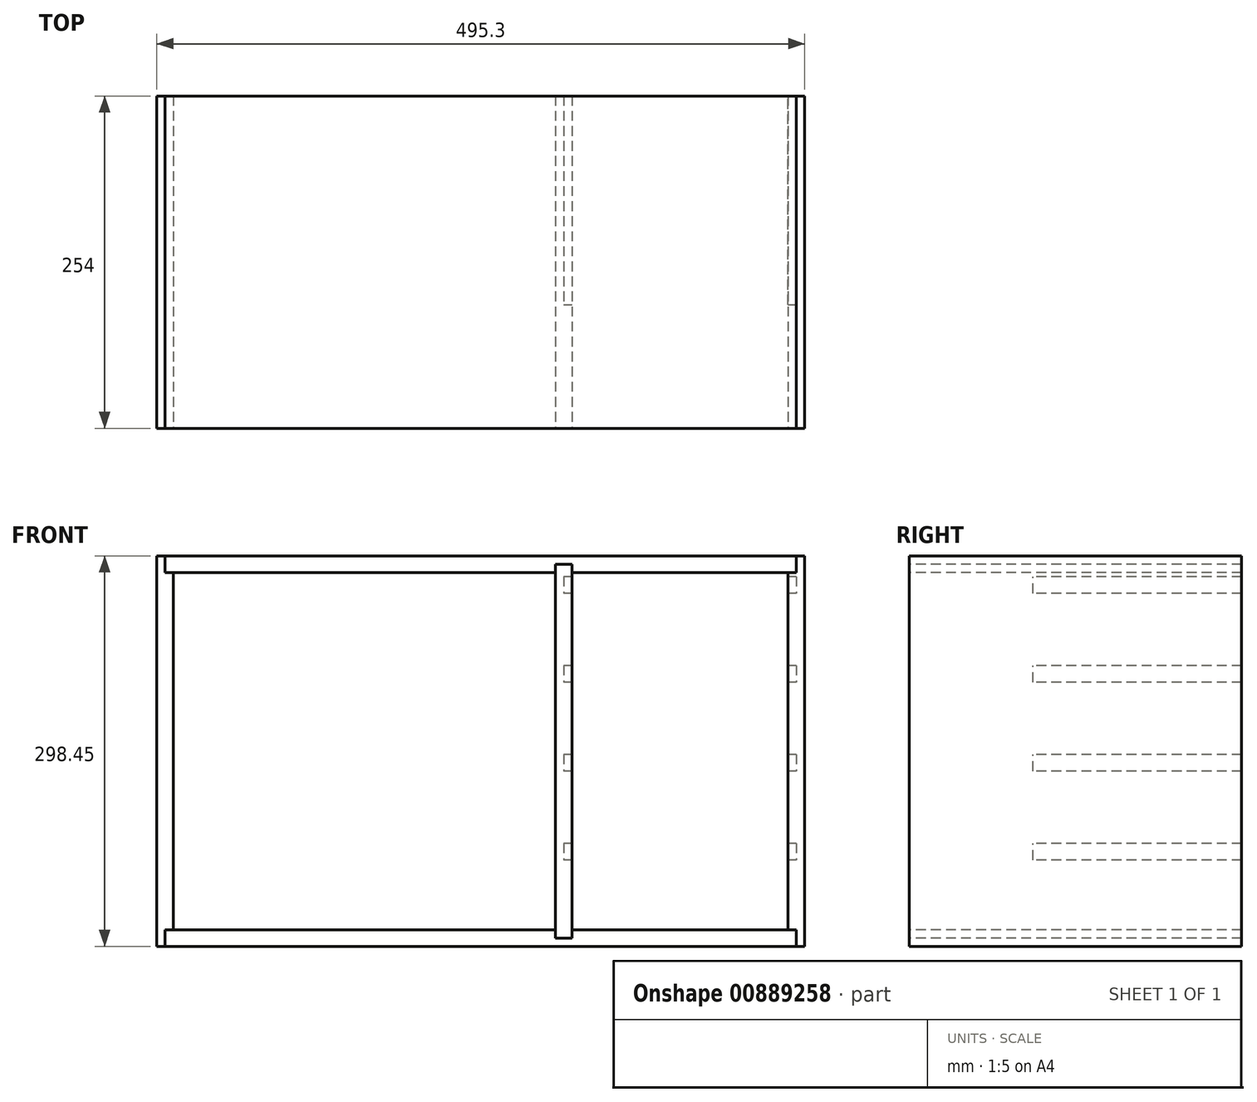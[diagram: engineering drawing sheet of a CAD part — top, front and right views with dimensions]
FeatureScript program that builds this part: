
annotation { "Feature Type Name" : "Feature", "Feature Type Description" : "" }
export const myFeature = defineFeature(function(context is Context, id is Id, definition is map)
    precondition{}
    {
        {
            var Q0;
            Q0=qCreatedBy(makeId("Front.planeOp"),FACE);
            var sketch = newSketch(context, id + "F0", { "sketchPlane" : qUnion([Q0])});
            skLineSegment(sketch, "E0.bottom", {"start": v(0, 0) * mm, "end": v(495.3, 0) * mm});
            skLineSegment(sketch, "E0.top", {"start": v(0, 298.45) * mm, "end": v(495.3, 298.45) * mm});
            skLineSegment(sketch, "E0.left", {"start": v(0, 0) * mm, "end": v(0, 298.45) * mm});
            skLineSegment(sketch, "E0.right", {"start": v(495.3, 0) * mm, "end": v(495.3, 298.45) * mm});
            skLineSegment(sketch, "E1.0", {"start": v(12.7, 285.75) * mm, "end": v(482.6, 285.75) * mm});
            skLineSegment(sketch, "E1.1", {"start": v(12.7, 12.7) * mm, "end": v(12.7, 285.75) * mm});
            skLineSegment(sketch, "E1.2", {"start": v(12.7, 12.7) * mm, "end": v(482.6, 12.7) * mm});
            skLineSegment(sketch, "E1.3", {"start": v(482.6, 12.7) * mm, "end": v(482.6, 285.75) * mm});
            skLineSegment(sketch, "E2", {"start": v(311.15, 12.7) * mm, "end": v(311.15, 285.75) * mm, "construction": true});
            skLineSegment(sketch, "E3.0", {"start": v(317.5, 12.7) * mm, "end": v(317.5, 285.75) * mm, "construction": true});
            skLineSegment(sketch, "E4.0", {"start": v(304.8, 12.7) * mm, "end": v(304.8, 285.75) * mm, "construction": true});
            skLineSegment(sketch, "E5", {"start": v(12.7, 44.45) * mm, "end": v(304.8, 44.45) * mm, "construction": true});
            skLineSegment(sketch, "E6.0.1.0", {"start": v(12.7, 76.2) * mm, "end": v(304.8, 76.2) * mm, "construction": true});
            skLineSegment(sketch, "E6.0.2.0", {"start": v(12.7, 107.95) * mm, "end": v(304.8, 107.95) * mm, "construction": true});
            skLineSegment(sketch, "E6.0.3.0", {"start": v(12.7, 139.7) * mm, "end": v(304.8, 139.7) * mm, "construction": true});
            skLineSegment(sketch, "E6.direction1", {"start": v(12.7, 44.45) * mm, "end": v(37.1, 44.45) * mm, "construction": true});
            skLineSegment(sketch, "E6.direction2", {"start": v(12.7, 44.45) * mm, "end": v(12.7, 76.2) * mm, "construction": true});
            skLineSegment(sketch, "E7.0.0.4", {"start": v(12.7, 171.45) * mm, "end": v(304.8, 171.45) * mm, "construction": true});
            skLineSegment(sketch, "E7.0.0.5", {"start": v(12.7, 203.2) * mm, "end": v(304.8, 203.2) * mm, "construction": true});
            skLineSegment(sketch, "E7.0.0.6", {"start": v(12.7, 234.95) * mm, "end": v(304.8, 234.95) * mm, "construction": true});
            skLineSegment(sketch, "E7.0.0.7", {"start": v(12.7, 266.7) * mm, "end": v(304.8, 266.7) * mm, "construction": true});
            skLineSegment(sketch, "E8", {"start": v(317.5, 69.85) * mm, "end": v(482.6, 69.85) * mm, "construction": true});
            skLineSegment(sketch, "E9.0.1.0", {"start": v(317.5, 127) * mm, "end": v(482.6, 127) * mm, "construction": true});
            skLineSegment(sketch, "E9.0.2.0", {"start": v(317.5, 184.15) * mm, "end": v(482.6, 184.15) * mm, "construction": true});
            skLineSegment(sketch, "E9.0.3.0", {"start": v(317.5, 241.3) * mm, "end": v(482.6, 241.3) * mm, "construction": true});
            skLineSegment(sketch, "E9.direction1", {"start": v(317.5, 69.85) * mm, "end": v(320.67, 69.85) * mm, "construction": true});
            skLineSegment(sketch, "E9.direction2", {"start": v(317.5, 69.85) * mm, "end": v(317.5, 127) * mm, "construction": true});
            skLineSegment(sketch, "E10", {"start": v(247.65, 12.7) * mm, "end": v(247.65, 332.22) * mm, "construction": true});
            skPoint(sketch, "E10.endSnap0", {"position": v(247.65, 298.45) * mm});
            skLineSegment(sketch, "E11", {"start": v(0, 149.22) * mm, "end": v(623.55, 149.23) * mm, "construction": true});
            skPoint(sketch, "E11.endSnap0", {"position": v(482.6, 149.22) * mm});
            skLineSegment(sketch, "E12.bottom", {"start": v(304.8, 12.7) * mm, "end": v(317.5, 12.7) * mm});
            skLineSegment(sketch, "E12.top", {"start": v(304.8, 6.35) * mm, "end": v(317.5, 6.35) * mm});
            skLineSegment(sketch, "E12.left", {"start": v(304.8, 12.7) * mm, "end": v(304.8, 6.35) * mm});
            skLineSegment(sketch, "E12.right", {"start": v(317.5, 12.7) * mm, "end": v(317.5, 6.35) * mm});
            skLineSegment(sketch, "E13.bottom", {"start": v(304.8, 285.75) * mm, "end": v(317.5, 285.75) * mm});
            skLineSegment(sketch, "E13.top", {"start": v(304.8, 292.1) * mm, "end": v(317.5, 292.1) * mm});
            skLineSegment(sketch, "E13.left", {"start": v(304.8, 285.75) * mm, "end": v(304.8, 292.1) * mm});
            skLineSegment(sketch, "E13.right", {"start": v(317.5, 285.75) * mm, "end": v(317.5, 292.1) * mm});
            skLineSegment(sketch, "E14.left", {"start": v(304.8, 292.1) * mm, "end": v(304.8, 6.35) * mm});
            skLineSegment(sketch, "E14.right", {"start": v(317.5, 292.1) * mm, "end": v(317.5, 6.35) * mm});
            skSolve(sketch);
        }
        {
            var Q0;
            Q0=qCreatedBy(makeId("Front.planeOp"),FACE);
            var sketch = newSketch(context, id + "F1", { "sketchPlane" : qUnion([Q0])});
            skLineSegment(sketch, "E15.bottom", {"start": v(0, 298.45) * mm, "end": v(6.35, 298.45) * mm});
            skLineSegment(sketch, "E15.top", {"start": v(0, 0) * mm, "end": v(6.35, 0) * mm});
            skLineSegment(sketch, "E15.left", {"start": v(0, 298.45) * mm, "end": v(0, 0) * mm});
            skLineSegment(sketch, "E15.right", {"start": v(12.7, 285.75) * mm, "end": v(12.7, 12.7) * mm});
            skLineSegment(sketch, "E16", {"start": v(6.35, 298.45) * mm, "end": v(6.35, 285.75) * mm});
            skLineSegment(sketch, "E17", {"start": v(6.35, 285.75) * mm, "end": v(12.7, 285.75) * mm});
            skPoint(sketch, "E18.orphan", {"position": v(12.7, 298.45) * mm});
            skLineSegment(sketch, "E19.top", {"start": v(12.7, 12.7) * mm, "end": v(6.35, 12.7) * mm});
            skLineSegment(sketch, "E19.right", {"start": v(6.35, 0) * mm, "end": v(6.35, 12.7) * mm});
            skSolve(sketch);
        }
        {
            var Q0;
            Q0 = qSketchRegion(id + "F1", true);
            extrude(context, id + "F2", {"entities" : qUnion([Q0]), "oppositeDirection" : true, "depth" : 254 * mm, "offsetDistance" : 25.4 * mm});
        }
        {
            var Q0;
            Q0=qCreatedBy(makeId("Front.planeOp"),FACE);
            var sketch = newSketch(context, id + "F3", { "sketchPlane" : qUnion([Q0])});
            skLineSegment(sketch, "E20", {"start": v(6.35, 0) * mm, "end": v(488.95, 0) * mm});
            skLineSegment(sketch, "E21", {"start": v(6.35, 0) * mm, "end": v(6.35, 12.7) * mm});
            skLineSegment(sketch, "E22", {"start": v(6.35, 12.7) * mm, "end": v(12.7, 12.7) * mm});
            skLineSegment(sketch, "E23", {"start": v(12.7, 12.7) * mm, "end": v(12.7, 12.7) * mm});
            skLineSegment(sketch, "E24", {"start": v(12.7, 12.7) * mm, "end": v(488.95, 12.7) * mm});
            skLineSegment(sketch, "E25", {"start": v(488.95, 0) * mm, "end": v(488.95, 12.7) * mm});
            skPoint(sketch, "E26.orphan", {"position": v(495.3, 0) * mm});
            skSolve(sketch);
        }
        {
            var Q0;
            Q0 = qSketchRegion(id + "F3", true);
            var Q1;
            Q1=makeQuery(id+"F2.opExtrude","CAP_FACE",FACE,{"disambiguationData":[OSD([sQuery(id+"F1.wireOp",EDGE,"E15.bottom"),sQuery(id+"F1.wireOp",EDGE,"E15.top"),sQuery(id+"F1.wireOp",EDGE,"E15.left"),sQuery(id+"F1.wireOp",EDGE,"E15.right"),sQuery(id+"F1.wireOp",EDGE,"E16"),sQuery(id+"F1.wireOp",EDGE,"E17"),sQuery(id+"F1.wireOp",EDGE,"E19.top"),sQuery(id+"F1.wireOp",EDGE,"E19.right")])],"isStart":false});
            extrude(context, id + "F4", {"entities" : qUnion([Q0]), "endBound" : BoundingType.UP_TO_SURFACE, "oppositeDirection" : true, "depth" : 25.4 * mm, "endBoundEntityFace" : qUnion([Q1]), "offsetDistance" : 25.4 * mm});
        }
        {
            var Q0;
            Q0=qCreatedBy(makeId("Front.planeOp"),FACE);
            var sketch = newSketch(context, id + "F5", { "sketchPlane" : qUnion([Q0])});
            skLineSegment(sketch, "E27.top", {"start": v(488.95, 298.45) * mm, "end": v(495.3, 298.45) * mm});
            skLineSegment(sketch, "E27.left", {"start": v(482.6, 12.7) * mm, "end": v(482.6, 285.75) * mm});
            skLineSegment(sketch, "E27.right", {"start": v(495.3, 0) * mm, "end": v(495.3, 298.45) * mm});
            skLineSegment(sketch, "E28.bottom", {"start": v(482.6, 285.75) * mm, "end": v(488.95, 285.75) * mm});
            skLineSegment(sketch, "E28.right", {"start": v(488.95, 285.75) * mm, "end": v(488.95, 298.45) * mm});
            skLineSegment(sketch, "E29", {"start": v(482.6, 12.7) * mm, "end": v(488.95, 12.7) * mm});
            skLineSegment(sketch, "E30", {"start": v(488.95, 12.7) * mm, "end": v(488.95, 0) * mm});
            skLineSegment(sketch, "E31", {"start": v(488.95, 0) * mm, "end": v(495.3, 0) * mm});
            skSolve(sketch);
        }
        {
            var Q0;
            Q0 = qSketchRegion(id + "F5", true);
            var Q1;
            Q1=makeQuery(id+"F4.opExtrude","CAP_FACE",FACE,{"disambiguationData":[OSD([sQuery(id+"F3.wireOp",EDGE,"E20"),sQuery(id+"F3.wireOp",EDGE,"E21"),sQuery(id+"F3.wireOp",EDGE,"E22"),sQuery(id+"F3.wireOp",EDGE,"E24"),sQuery(id+"F3.wireOp",EDGE,"E25")])],"isStart":false});
            extrude(context, id + "F6", {"entities" : qUnion([Q0]), "endBound" : BoundingType.UP_TO_SURFACE, "oppositeDirection" : true, "depth" : 25.4 * mm, "endBoundEntityFace" : qUnion([Q1]), "offsetDistance" : 25.4 * mm});
        }
        {
            var Q0;
            Q0=qCreatedBy(makeId("Front.planeOp"),FACE);
            var sketch = newSketch(context, id + "F7", { "sketchPlane" : qUnion([Q0])});
            skLineSegment(sketch, "E32.bottom", {"start": v(6.35, 285.75) * mm, "end": v(488.95, 285.75) * mm});
            skLineSegment(sketch, "E32.top", {"start": v(6.35, 298.45) * mm, "end": v(488.95, 298.45) * mm});
            skLineSegment(sketch, "E32.left", {"start": v(6.35, 285.75) * mm, "end": v(6.35, 298.45) * mm});
            skLineSegment(sketch, "E32.right", {"start": v(488.95, 285.75) * mm, "end": v(488.95, 298.45) * mm});
            skSolve(sketch);
        }
        {
            var Q0;
            Q0 = qSketchRegion(id + "F7", true);
            var Q1;
            Q1=makeQuery(id+"F4.opExtrude","CAP_FACE",FACE,{"disambiguationData":[OSD([sQuery(id+"F3.wireOp",EDGE,"E20"),sQuery(id+"F3.wireOp",EDGE,"E21"),sQuery(id+"F3.wireOp",EDGE,"E22"),sQuery(id+"F3.wireOp",EDGE,"E24"),sQuery(id+"F3.wireOp",EDGE,"E25")])],"isStart":false});
            extrude(context, id + "F8", {"entities" : qUnion([Q0]), "endBound" : BoundingType.UP_TO_SURFACE, "oppositeDirection" : true, "depth" : 25.4 * mm, "endBoundEntityFace" : qUnion([Q1]), "offsetDistance" : 25.4 * mm});
        }
        {
            var Q0;
            Q0=makeQuery(id+"F0.imprint","IMPRINT",FACE,{"disambiguationData":[TD([[makeQuery(id+"F0.imprint","IMPRINT",EDGE,{"derivedFrom":sQuery(id+"F0.wireOp",EDGE,"E13.top")}),-1.0]])]});
            var Q1;
            Q1=makeQuery(id+"F0.imprint","IMPRINT",FACE,{"disambiguationData":[TD([[makeQuery(id+"F0.imprint","IMPRINT",EDGE,{"derivedFrom":sQuery(id+"F0.wireOp",EDGE,"E12.top")}),1.0]])]});
            extrude(context, id + "F9", {"entities" : qUnion([Q0, Q1]), "operationType" : NewBodyOperationType.REMOVE, "endBound" : BoundingType.THROUGH_ALL, "oppositeDirection" : true, "depth" : 25.4 * mm, "offsetDistance" : 25.4 * mm});
        }
        {
            var Q0;
            {var subQ2=sQuery(id+"F0.wireOp",EDGE,"E14.left");Q0=makeQuery(id+"F0.imprint","IMPRINT",FACE,{"disambiguationData":[TD([[makeQuery(id+"F0.imprint","IMPRINT",EDGE,{"derivedFrom":subQ2}),1.0]])]});}
            var Q1;
            Q1=makeQuery(id+"F0.imprint","IMPRINT",FACE,{"disambiguationData":[TD([[makeQuery(id+"F0.imprint","IMPRINT",EDGE,{"derivedFrom":sQuery(id+"F0.wireOp",EDGE,"E13.top")}),-1.0]])]});
            var Q2;
            Q2=makeQuery(id+"F0.imprint","IMPRINT",FACE,{"disambiguationData":[TD([[makeQuery(id+"F0.imprint","IMPRINT",EDGE,{"derivedFrom":sQuery(id+"F0.wireOp",EDGE,"E12.top")}),1.0]])]});
            var Q3;
            Q3=makeQuery(id+"F4.opExtrude","CAP_FACE",FACE,{"disambiguationData":[OSD([sQuery(id+"F3.wireOp",EDGE,"E20"),sQuery(id+"F3.wireOp",EDGE,"E21"),sQuery(id+"F3.wireOp",EDGE,"E22"),sQuery(id+"F3.wireOp",EDGE,"E24"),sQuery(id+"F3.wireOp",EDGE,"E25")])],"isStart":false});
            extrude(context, id + "F10", {"entities" : qUnion([Q0, Q1, Q2]), "endBound" : BoundingType.UP_TO_SURFACE, "oppositeDirection" : true, "depth" : 25.4 * mm, "endBoundEntityFace" : qUnion([Q3]), "offsetDistance" : 25.4 * mm});
        }
        {
            var Q0;
            {var subQ2=sQuery(id+"F0.wireOp",EDGE,"E14.left");Q0=makeQuery(id+"F0.imprint","IMPRINT",FACE,{"disambiguationData":[TD([[makeQuery(id+"F0.imprint","IMPRINT",EDGE,{"derivedFrom":subQ2}),1.0]])]});}
            var sketch = newSketch(context, id + "F11", { "sketchPlane" : qUnion([Q0])});
            skLineSegment(sketch, "E33.bottom", {"start": v(311.15, 66.04) * mm, "end": v(488.95, 66.04) * mm});
            skLineSegment(sketch, "E33.top", {"start": v(311.15, 78.74) * mm, "end": v(488.95, 78.74) * mm});
            skLineSegment(sketch, "E33.left", {"start": v(311.15, 66.04) * mm, "end": v(311.15, 78.74) * mm});
            skLineSegment(sketch, "E33.right", {"start": v(488.95, 66.04) * mm, "end": v(488.95, 78.74) * mm});
            skLineSegment(sketch, "E34.0.1.0", {"start": v(311.15, 146.69) * mm, "end": v(488.95, 146.69) * mm});
            skLineSegment(sketch, "E34.0.1.1", {"start": v(311.15, 133.99) * mm, "end": v(488.95, 133.99) * mm});
            skLineSegment(sketch, "E34.0.1.2", {"start": v(488.95, 133.99) * mm, "end": v(488.95, 146.69) * mm});
            skLineSegment(sketch, "E34.0.1.3", {"start": v(311.15, 133.99) * mm, "end": v(311.15, 146.69) * mm});
            skLineSegment(sketch, "E34.0.2.0", {"start": v(311.15, 214.63) * mm, "end": v(488.95, 214.63) * mm});
            skLineSegment(sketch, "E34.0.2.1", {"start": v(311.15, 201.93) * mm, "end": v(488.95, 201.93) * mm});
            skLineSegment(sketch, "E34.0.2.2", {"start": v(488.95, 201.93) * mm, "end": v(488.95, 214.63) * mm});
            skLineSegment(sketch, "E34.0.2.3", {"start": v(311.15, 201.93) * mm, "end": v(311.15, 214.63) * mm});
            skLineSegment(sketch, "E34.direction1", {"start": v(311.15, 66.04) * mm, "end": v(336.55, 66.04) * mm, "construction": true});
            skLineSegment(sketch, "E34.direction2", {"start": v(311.15, 66.04) * mm, "end": v(311.15, 133.99) * mm, "construction": true});
            skLineSegment(sketch, "E35.0.0.3", {"start": v(311.15, 282.58) * mm, "end": v(488.95, 282.58) * mm});
            skLineSegment(sketch, "E35.3.0.3", {"start": v(311.15, 269.88) * mm, "end": v(488.95, 269.88) * mm});
            skLineSegment(sketch, "E35.6.0.3", {"start": v(488.95, 269.88) * mm, "end": v(488.95, 282.58) * mm});
            skLineSegment(sketch, "E35.9.0.3", {"start": v(311.15, 269.88) * mm, "end": v(311.15, 282.58) * mm});
            skSolve(sketch);
        }
        {
            var Q0;
            Q0 = qSketchRegion(id + "F11", true);
            var Q1;
            Q1=makeQuery(id+"F10.opExtrude","CAP_FACE",FACE,{"disambiguationData":[OSD([sQuery(id+"F0.wireOp",EDGE,"E12.top"),sQuery(id+"F0.wireOp",EDGE,"E12.left"),sQuery(id+"F0.wireOp",EDGE,"E12.right"),sQuery(id+"F0.wireOp",EDGE,"E13.top"),sQuery(id+"F0.wireOp",EDGE,"E13.left"),sQuery(id+"F0.wireOp",EDGE,"E13.right"),sQuery(id+"F0.wireOp",EDGE,"E14.left"),sQuery(id+"F0.wireOp",EDGE,"E14.right")])],"isStart":false});
            extrude(context, id + "F12", {"entities" : qUnion([Q0]), "operationType" : NewBodyOperationType.REMOVE, "endBound" : BoundingType.UP_TO_SURFACE, "oppositeDirection" : true, "depth" : 25.4 * mm, "endBoundEntityFace" : qUnion([Q1]), "offsetDistance" : 25.4 * mm, "hasSecondDirection" : true, "secondDirectionOppositeDirection" : true, "secondDirectionDepth" : 94.49 * mm});
        }
    });
